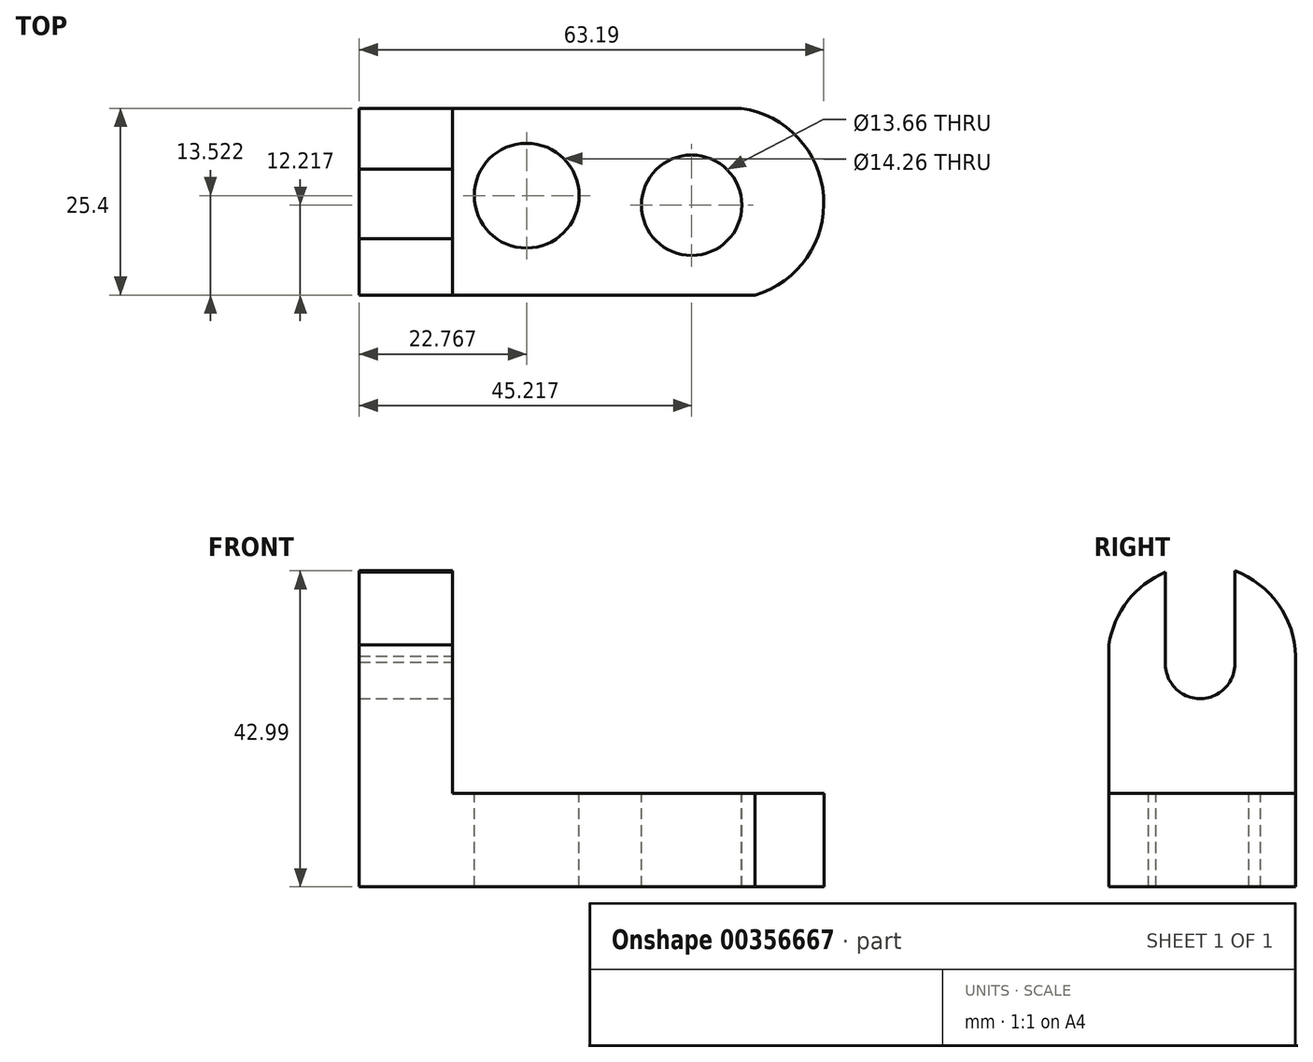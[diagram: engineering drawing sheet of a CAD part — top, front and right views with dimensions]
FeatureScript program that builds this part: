
annotation { "Feature Type Name" : "Feature", "Feature Type Description" : "" }
export const myFeature = defineFeature(function(context is Context, id is Id, definition is map)
    precondition{}
    {
        {
            var Q0;
            Q0=qCreatedBy(makeId("Front.planeOp"),FACE);
            var sketch = newSketch(context, id + "F0", { "sketchPlane" : qUnion([Q0])});
            skLineSegment(sketch, "E0", {"start": v(-38.43, 35.67) * mm, "end": v(-38.43, -8.78) * mm});
            skLineSegment(sketch, "E1", {"start": v(-38.43, -8.78) * mm, "end": v(25.07, -8.78) * mm});
            skLineSegment(sketch, "E2", {"start": v(25.07, -8.78) * mm, "end": v(25.07, 3.92) * mm});
            skLineSegment(sketch, "E3", {"start": v(25.07, 3.92) * mm, "end": v(-25.73, 3.92) * mm});
            skLineSegment(sketch, "E4", {"start": v(-25.73, 3.92) * mm, "end": v(-25.73, 35.67) * mm});
            skLineSegment(sketch, "E5", {"start": v(-25.73, 35.67) * mm, "end": v(-38.43, 35.67) * mm});
            skSolve(sketch);
        }
        {
            var Q0;
            Q0=makeQuery(id+"F0.imprint","IMPRINT",FACE,{"disambiguationData":[TD([[makeQuery(id+"F0.imprint","IMPRINT",EDGE,{"derivedFrom":sQuery(id+"F0.wireOp",EDGE,"E0")}),1.0]])]});
            extrude(context, id + "F1", {"entities" : qUnion([Q0]), "depth" : 25.4 * mm});
        }
        {
            var Q0;
            Q0=makeQuery(id+"F1.opExtrude","SWEPT_FACE",FACE,{"disambiguationData":[OSD([sQuery(id+"F0.wireOp",EDGE,"E4")])]});
            var sketch = newSketch(context, id + "F2", { "sketchPlane" : qUnion([Q0])});
            skArc(sketch, "E6", {"start": v(0, 22.58) * mm, "mid": v(-11.98, 35) * mm, "end": v(-25.4, 24.15) * mm});
            skSolve(sketch);
        }
        {
            var Q0;
            {var subQ0=sQuery(id+"F2.wireOp",EDGE,"E6");Q0=makeQuery(id+"F2.imprint","IMPRINT",FACE,{"disambiguationData":[TD([[makeQuery(id+"F2.imprint","IMPRINT",EDGE,{"derivedFrom":subQ0}),-1.0]])]});}
            extrude(context, id + "F3", {"entities" : qUnion([Q0]), "operationType" : NewBodyOperationType.REMOVE, "oppositeDirection" : true, "depth" : 25.4 * mm});
        }
        {
            var Q0;
            Q0=makeQuery(id+"F1.opExtrude","SWEPT_FACE",FACE,{"disambiguationData":[OSD([sQuery(id+"F0.wireOp",EDGE,"E4")])]});
            var sketch = newSketch(context, id + "F4", { "sketchPlane" : qUnion([Q0])});
            skLineSegment(sketch, "E7", {"start": v(-17.7, 34.03) * mm, "end": v(-17.7, 21.8) * mm});
            skLineSegment(sketch, "E8", {"start": v(-8.28, 34.2) * mm, "end": v(-8.28, 21.54) * mm});
            skArc(sketch, "E9", {"start": v(-17.7, 21.8) * mm, "mid": v(-13.13, 16.82) * mm, "end": v(-8.28, 21.54) * mm});
            skSolve(sketch);
        }
        {
            var Q0;
            {var subQ0=sQuery(id+"F4.wireOp",EDGE,"E7");Q0=makeQuery(id+"F4.imprint","IMPRINT",FACE,{"disambiguationData":[TD([[makeQuery(id+"F4.imprint","IMPRINT",EDGE,{"derivedFrom":subQ0}),1.0]])]});}
            extrude(context, id + "F5", {"entities" : qUnion([Q0]), "operationType" : NewBodyOperationType.REMOVE, "oppositeDirection" : true, "depth" : 25.4 * mm});
        }
        {
            var Q0;
            Q0=makeQuery(id+"F1.opExtrude","SWEPT_FACE",FACE,{"disambiguationData":[OSD([sQuery(id+"F0.wireOp",EDGE,"E3")])]});
            var sketch = newSketch(context, id + "F6", { "sketchPlane" : qUnion([Q0])});
            skArc(sketch, "E10", {"start": v(15.4, -25.4) * mm, "mid": v(24.73, -11.96) * mm, "end": v(13.57, 0) * mm});
            skCircle(sketch, "E11", {"center": v(-15.66, -11.88) * mm, "radius": 7.13 * mm});
            skCircle(sketch, "E12", {"center": v(6.79, -13.18) * mm, "radius": 6.83 * mm});
            skSolve(sketch);
        }
        {
            var Q0;
            Q0=makeQuery(id+"F6.imprint","IMPRINT",FACE,{"disambiguationData":[TD([[makeQuery(id+"F6.imprint","IMPRINT",EDGE,{"derivedFrom":sQuery(id+"F6.wireOp",EDGE,"E11")}),1.0]])]});
            var Q1;
            Q1=makeQuery(id+"F6.imprint","IMPRINT",FACE,{"disambiguationData":[TD([[makeQuery(id+"F6.imprint","IMPRINT",EDGE,{"derivedFrom":sQuery(id+"F6.wireOp",EDGE,"E12")}),1.0]])]});
            var Q2;
            {var subQ0=sQuery(id+"F6.wireOp",EDGE,"E10");Q2=makeQuery(id+"F6.imprint","IMPRINT",FACE,{"disambiguationData":[TD([[makeQuery(id+"F6.imprint","IMPRINT",EDGE,{"derivedFrom":subQ0}),-1.0]])]});}
            extrude(context, id + "F7", {"entities" : qUnion([Q0, Q1, Q2]), "operationType" : NewBodyOperationType.REMOVE, "oppositeDirection" : true, "depth" : 25.4 * mm});
        }
    });
